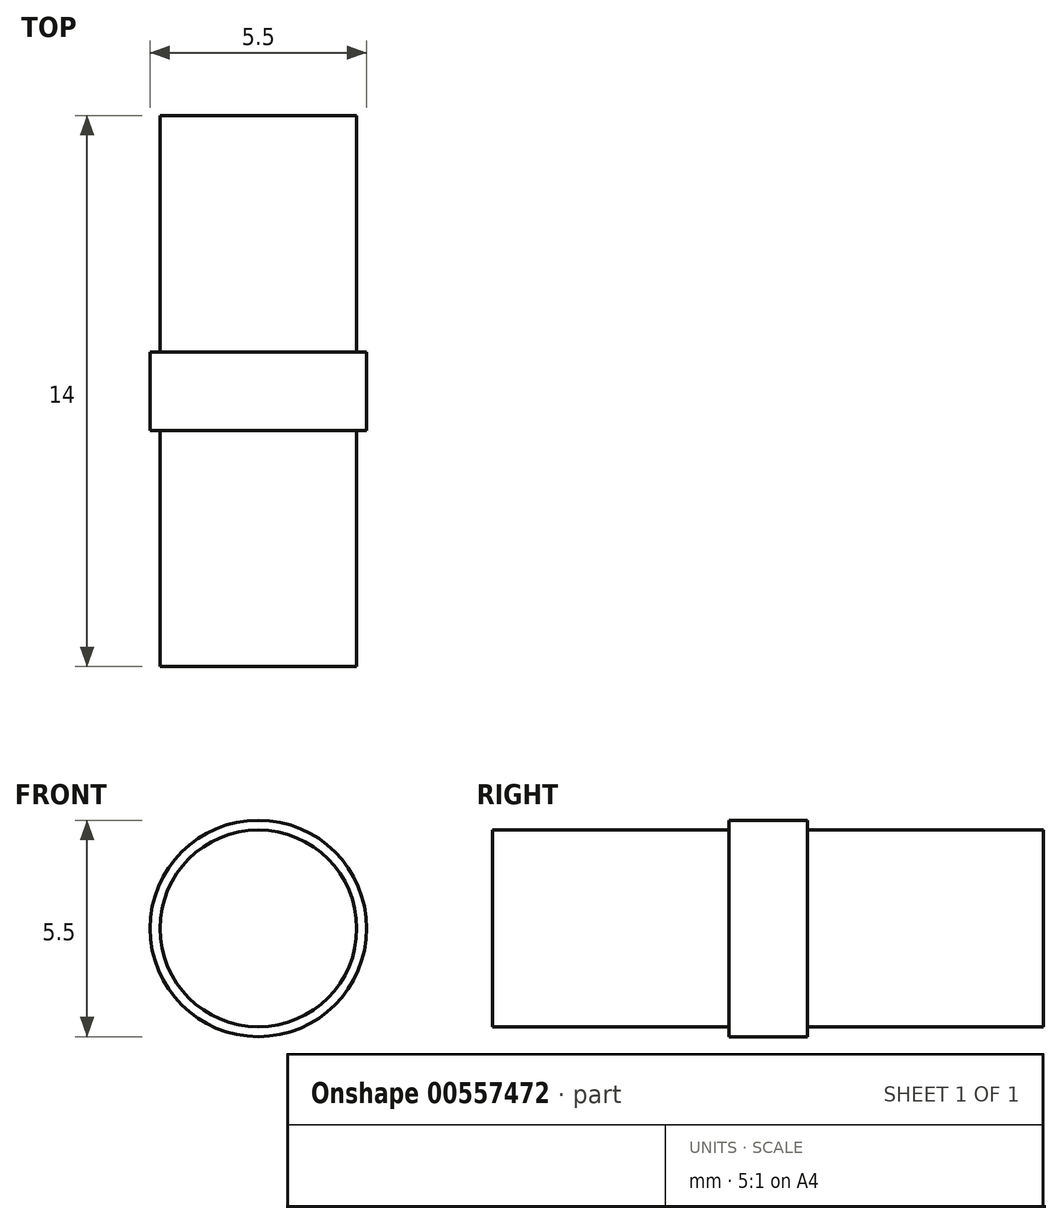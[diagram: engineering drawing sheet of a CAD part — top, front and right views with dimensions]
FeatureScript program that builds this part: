
annotation { "Feature Type Name" : "Feature", "Feature Type Description" : "" }
export const myFeature = defineFeature(function(context is Context, id is Id, definition is map)
    precondition{}
    {
        {
            var Q0;
            Q0=qCreatedBy(makeId("Front.planeOp"),FACE);
            var sketch = newSketch(context, id + "F0", { "sketchPlane" : qUnion([Q0])});
            skCircle(sketch, "E0", {"center": v(0, 0) * mm, "radius": 2.75 * mm});
            skSolve(sketch);
        }
        {
            var Q0;
            Q0 = qSketchRegion(id + "F0", true);
            extrude(context, id + "F1", {"entities" : qUnion([Q0]), "endBound" : BoundingType.SYMMETRIC, "depth" : 14 * mm, "offsetDistance" : 25 * mm});
        }
        {
            var Q0;
            Q0=makeQuery(id+"F1.opExtrude","CAP_FACE",FACE,{"disambiguationData":[OSD([sQuery(id+"F0.wireOp",EDGE,"E0")])],"isStart":false});
            var sketch = newSketch(context, id + "F2", { "sketchPlane" : qUnion([Q0])});
            skCircle(sketch, "E1", {"center": v(0, 0) * mm, "radius": 2.75 * mm});
            skCircle(sketch, "E2", {"center": v(0, 0) * mm, "radius": 2.5 * mm});
            skSolve(sketch);
        }
        {
            var Q0;
            Q0 = qSketchRegion(id + "F2", true);
            extrude(context, id + "F3", {"entities" : qUnion([Q0]), "operationType" : NewBodyOperationType.REMOVE, "oppositeDirection" : true, "depth" : 6 * mm, "offsetDistance" : 25 * mm});
        }
        {
            var Q0;
            Q0=makeQuery(id+"F1.opExtrude","CAP_FACE",FACE,{"disambiguationData":[OSD([sQuery(id+"F0.wireOp",EDGE,"E0")])],"isStart":true});
            var sketch = newSketch(context, id + "F4", { "sketchPlane" : qUnion([Q0])});
            skCircle(sketch, "E3", {"center": v(0, 0) * mm, "radius": 2.75 * mm});
            skCircle(sketch, "E4", {"center": v(0, 0) * mm, "radius": 2.5 * mm});
            skSolve(sketch);
        }
        {
            var Q0;
            Q0 = qSketchRegion(id + "F4", true);
            extrude(context, id + "F5", {"entities" : qUnion([Q0]), "operationType" : NewBodyOperationType.REMOVE, "oppositeDirection" : true, "depth" : 6 * mm, "offsetDistance" : 25 * mm});
        }
    });
